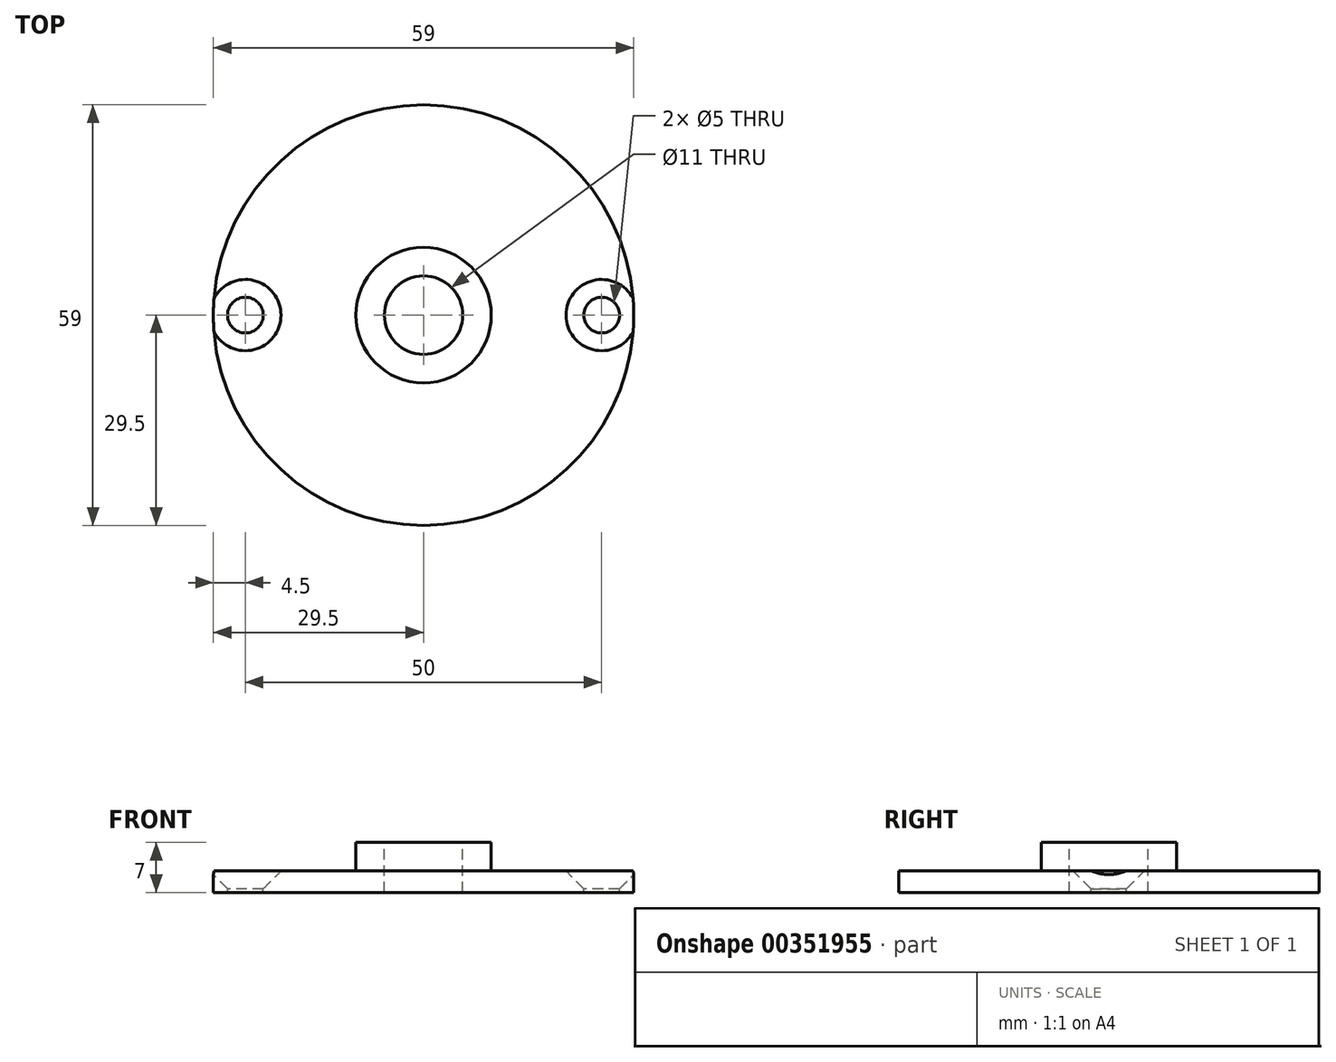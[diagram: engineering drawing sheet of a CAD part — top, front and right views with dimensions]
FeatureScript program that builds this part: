
annotation { "Feature Type Name" : "Feature", "Feature Type Description" : "" }
export const myFeature = defineFeature(function(context is Context, id is Id, definition is map)
    precondition{}
    {
        {
            var Q0;
            Q0=qCreatedBy(makeId("Right.planeOp"),FACE);
            var sketch = newSketch(context, id + "F0", { "sketchPlane" : qUnion([Q0])});
            skLineSegment(sketch, "E0", {"start": v(-29.5, 0) * mm, "end": v(-29.5, 3) * mm});
            skLineSegment(sketch, "E1", {"start": v(-29.5, 3) * mm, "end": v(-9.5, 3) * mm});
            skLineSegment(sketch, "E2", {"start": v(-9.5, 3) * mm, "end": v(-9.5, 7) * mm});
            skLineSegment(sketch, "E3", {"start": v(-9.5, 7) * mm, "end": v(-5.5, 7) * mm});
            skLineSegment(sketch, "E4", {"start": v(-5.5, 7) * mm, "end": v(-5.5, 0) * mm});
            skLineSegment(sketch, "E5", {"start": v(-5.5, 0) * mm, "end": v(-29.5, 0) * mm});
            skLineSegment(sketch, "E6", {"start": v(0, 28.76) * mm, "end": v(0, -7.12) * mm, "construction": true});
            skSolve(sketch);
        }
        {
            var Q0;
            Q0 = qSketchRegion(id + "F0", true);
            var Q1;
            Q1=sQuery(id+"F0.wireOp",EDGE,"E6");
            revolve(context, id + "F1", {"entities" : qUnion([Q0]), "axis" : qUnion([Q1]), "revolveType" : RevolveType.FULL});
        }
        {
            var Q0;
            Q0=makeQuery(id+"F1.opRevolve","SWEPT_FACE",FACE,{"disambiguationData":[OSD([sQuery(id+"F0.wireOp",EDGE,"E1")])]});
            var sketch = newSketch(context, id + "F2", { "sketchPlane" : qUnion([Q0])});
            skPoint(sketch, "E7", {"position": v(-25, 0) * mm});
            skPoint(sketch, "E8.MirrorP", {"position": v(25, 0) * mm});
            skSolve(sketch);
        }
        {
            var Q0;
            Q0=sQuery(id+"F2.wireOp",VERTEX,"E7");
            var Q1;
            Q1=sQuery(id+"F2.wireOp",VERTEX,"E8.MirrorP");
            var Q2;
            Q2=makeQuery(id+"F1.opRevolve","SWEPT_BODY",BODY,{"disambiguationData":[OSD([sQuery(id+"F0.wireOp",EDGE,"E0"),sQuery(id+"F0.wireOp",EDGE,"E1"),sQuery(id+"F0.wireOp",EDGE,"E2"),sQuery(id+"F0.wireOp",EDGE,"E3"),sQuery(id+"F0.wireOp",EDGE,"E4"),sQuery(id+"F0.wireOp",EDGE,"E5")])]});
            hole(context, id + "F3", {"style" : HoleStyle.C_SINK, "endStyle" : HoleEndStyle.THROUGH, "holeDiameter" : 5 * mm, "cSinkDiameter" : 10 * mm, "cSinkAngle" : 90 * degree, "isTappedThrough" : true, "tappedDepth" : 12 * mm, "tapClearance" : 3, "locations" : qUnion([Q0, Q1]), "scope" : qUnion([Q2])});
        }
    });
